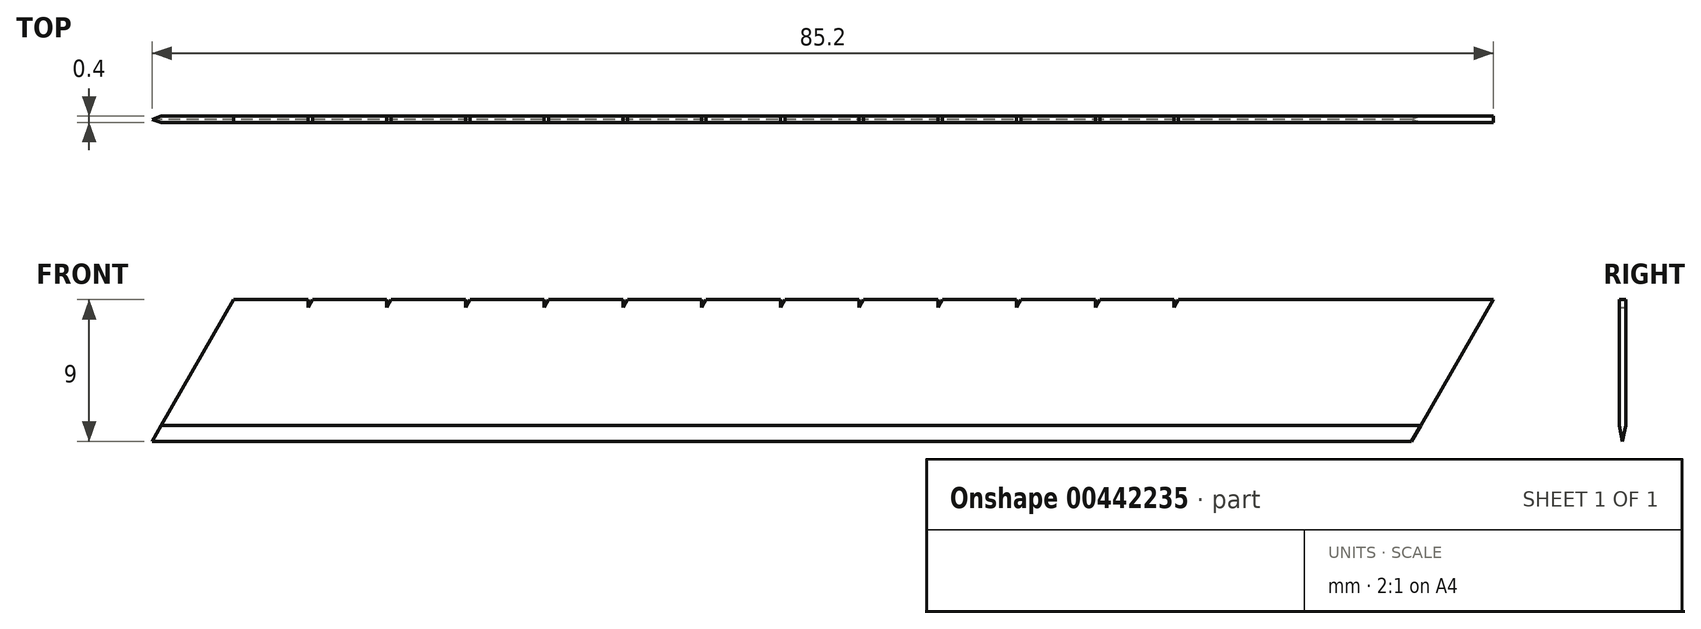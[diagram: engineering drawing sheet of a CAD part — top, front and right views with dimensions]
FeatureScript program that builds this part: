
annotation { "Feature Type Name" : "Feature", "Feature Type Description" : "" }
export const myFeature = defineFeature(function(context is Context, id is Id, definition is map)
    precondition{}
    {
        {
            var Q0;
            Q0=qCreatedBy(makeId("Front.planeOp"),FACE);
            var sketch = newSketch(context, id + "F0", { "sketchPlane" : qUnion([Q0])});
            skLineSegment(sketch, "E0.top", {"start": v(0, 0) * mm, "end": v(80, 0) * mm});
            skLineSegment(sketch, "E0.left", {"start": v(5.2, 9) * mm, "end": v(0, 0) * mm});
            skLineSegment(sketch, "E0.right", {"start": v(85.2, 9) * mm, "end": v(80, 0) * mm});
            skLineSegment(sketch, "E1", {"start": v(5.2, 9) * mm, "end": v(9.9, 9) * mm});
            skLineSegment(sketch, "E2", {"start": v(9.9, 9) * mm, "end": v(9.9, 8.5) * mm});
            skLineSegment(sketch, "E3", {"start": v(9.9, 8.5) * mm, "end": v(10.2, 9) * mm});
            skLineSegment(sketch, "E4.1.0.0", {"start": v(10.2, 9) * mm, "end": v(14.9, 9) * mm});
            skLineSegment(sketch, "E4.1.0.1", {"start": v(14.9, 9) * mm, "end": v(14.9, 8.5) * mm});
            skLineSegment(sketch, "E4.1.0.2", {"start": v(14.9, 8.5) * mm, "end": v(15.2, 9) * mm});
            skLineSegment(sketch, "E4.2.0.0", {"start": v(15.2, 9) * mm, "end": v(19.9, 9) * mm});
            skLineSegment(sketch, "E4.2.0.1", {"start": v(19.9, 9) * mm, "end": v(19.9, 8.5) * mm});
            skLineSegment(sketch, "E4.2.0.2", {"start": v(19.9, 8.5) * mm, "end": v(20.2, 9) * mm});
            skLineSegment(sketch, "E4.direction1", {"start": v(5.2, 9) * mm, "end": v(10.2, 9) * mm, "construction": true});
            skLineSegment(sketch, "E5.0.3.0", {"start": v(20.2, 9) * mm, "end": v(24.9, 9) * mm});
            skLineSegment(sketch, "E5.3.3.0", {"start": v(24.9, 9) * mm, "end": v(24.9, 8.5) * mm});
            skLineSegment(sketch, "E5.6.3.0", {"start": v(24.9, 8.5) * mm, "end": v(25.2, 9) * mm});
            skLineSegment(sketch, "E5.0.4.0", {"start": v(25.2, 9) * mm, "end": v(29.9, 9) * mm});
            skLineSegment(sketch, "E5.3.4.0", {"start": v(29.9, 9) * mm, "end": v(29.9, 8.5) * mm});
            skLineSegment(sketch, "E5.6.4.0", {"start": v(29.9, 8.5) * mm, "end": v(30.2, 9) * mm});
            skLineSegment(sketch, "E5.0.5.0", {"start": v(30.2, 9) * mm, "end": v(34.9, 9) * mm});
            skLineSegment(sketch, "E5.3.5.0", {"start": v(34.9, 9) * mm, "end": v(34.9, 8.5) * mm});
            skLineSegment(sketch, "E5.6.5.0", {"start": v(34.9, 8.5) * mm, "end": v(35.2, 9) * mm});
            skLineSegment(sketch, "E5.0.6.0", {"start": v(35.2, 9) * mm, "end": v(39.9, 9) * mm});
            skLineSegment(sketch, "E5.3.6.0", {"start": v(39.9, 9) * mm, "end": v(39.9, 8.5) * mm});
            skLineSegment(sketch, "E5.6.6.0", {"start": v(39.9, 8.5) * mm, "end": v(40.2, 9) * mm});
            skLineSegment(sketch, "E5.0.7.0", {"start": v(40.2, 9) * mm, "end": v(44.9, 9) * mm});
            skLineSegment(sketch, "E5.3.7.0", {"start": v(44.9, 9) * mm, "end": v(44.9, 8.5) * mm});
            skLineSegment(sketch, "E5.6.7.0", {"start": v(44.9, 8.5) * mm, "end": v(45.2, 9) * mm});
            skLineSegment(sketch, "E5.0.8.0", {"start": v(45.2, 9) * mm, "end": v(49.9, 9) * mm});
            skLineSegment(sketch, "E5.3.8.0", {"start": v(49.9, 9) * mm, "end": v(49.9, 8.5) * mm});
            skLineSegment(sketch, "E5.6.8.0", {"start": v(49.9, 8.5) * mm, "end": v(50.2, 9) * mm});
            skLineSegment(sketch, "E5.0.9.0", {"start": v(50.2, 9) * mm, "end": v(54.9, 9) * mm});
            skLineSegment(sketch, "E5.3.9.0", {"start": v(54.9, 9) * mm, "end": v(54.9, 8.5) * mm});
            skLineSegment(sketch, "E5.6.9.0", {"start": v(54.9, 8.5) * mm, "end": v(55.2, 9) * mm});
            skLineSegment(sketch, "E5.0.10.0", {"start": v(55.2, 9) * mm, "end": v(59.9, 9) * mm});
            skLineSegment(sketch, "E5.3.10.0", {"start": v(59.9, 9) * mm, "end": v(59.9, 8.5) * mm});
            skLineSegment(sketch, "E5.6.10.0", {"start": v(59.9, 8.5) * mm, "end": v(60.2, 9) * mm});
            skLineSegment(sketch, "E5.0.11.0", {"start": v(60.2, 9) * mm, "end": v(64.9, 9) * mm});
            skLineSegment(sketch, "E5.3.11.0", {"start": v(64.9, 9) * mm, "end": v(64.9, 8.5) * mm});
            skLineSegment(sketch, "E5.6.11.0", {"start": v(64.9, 8.5) * mm, "end": v(65.2, 9) * mm});
            skLineSegment(sketch, "E6", {"start": v(65.2, 9) * mm, "end": v(85.2, 9) * mm});
            skSolve(sketch);
        }
        {
            var Q0;
            Q0 = qSketchRegion(id + "F0", true);
            extrude(context, id + "F1", {"entities" : qUnion([Q0]), "endBound" : BoundingType.SYMMETRIC, "depth" : 0.4 * mm});
        }
        {
            var Q0;
            Q0=makeQuery(id+"F1.opExtrude","CAP_EDGE",EDGE,{"disambiguationData":[OSD([sQuery(id+"F0.wireOp",EDGE,"E0.top")])],"isStart":false});
            var Q1;
            Q1=makeQuery(id+"F1.opExtrude","CAP_EDGE",EDGE,{"disambiguationData":[OSD([sQuery(id+"F0.wireOp",EDGE,"E0.top")])],"isStart":true});
            chamfer(context, id + "F2", {"entities" : qUnion([Q0, Q1]), "chamferType" : ChamferType.TWO_OFFSETS, "width1" : 1 * mm, "oppositeDirection" : false, "width2" : 0.2 * mm, "tangentPropagation" : true});
        }
    });
